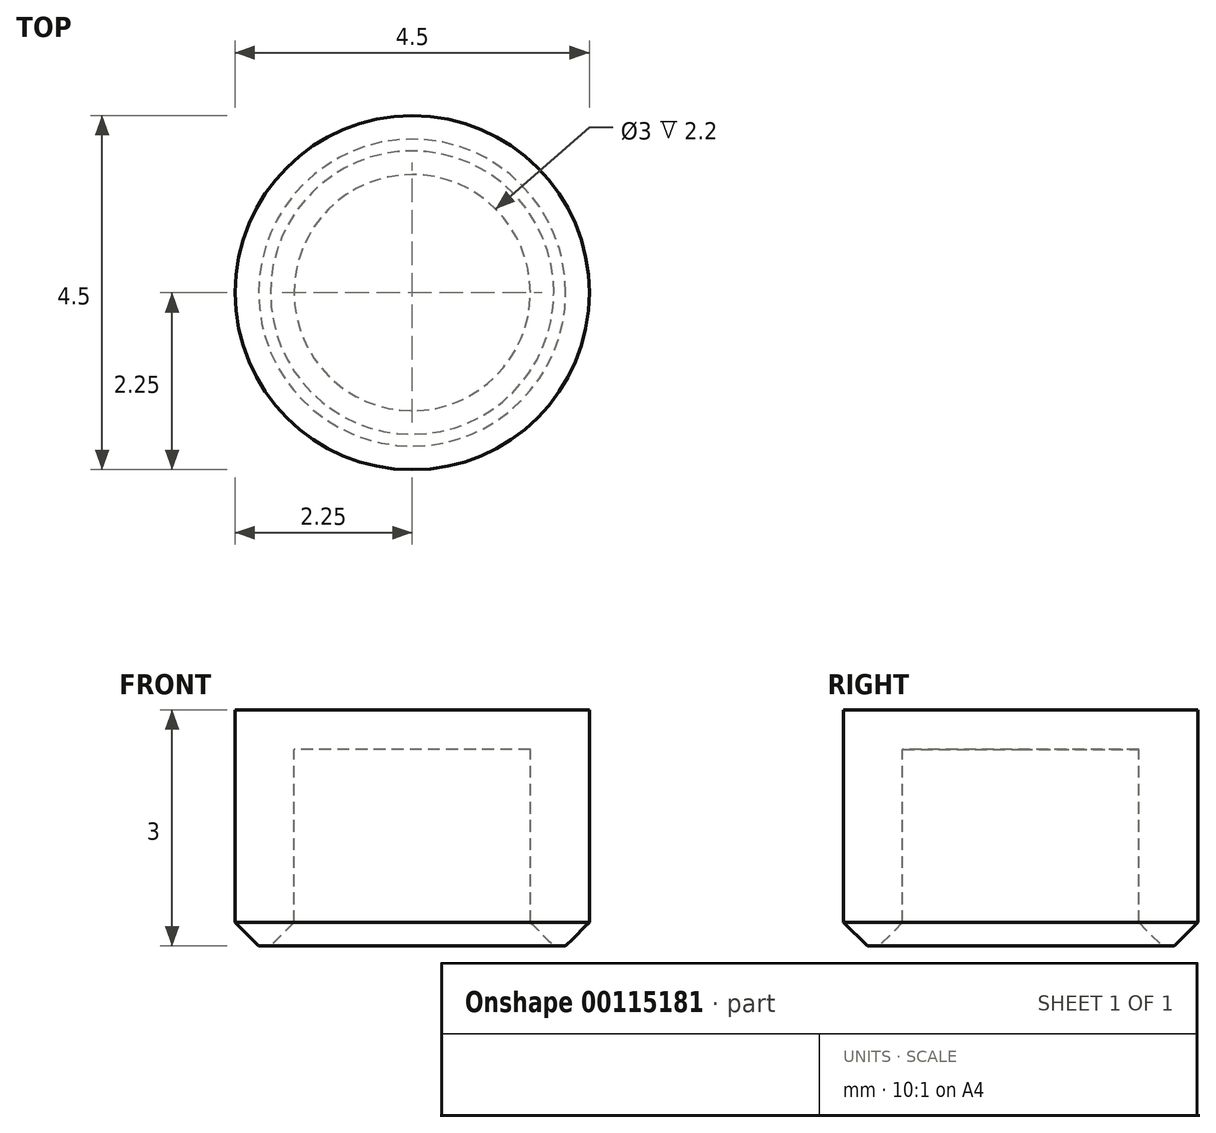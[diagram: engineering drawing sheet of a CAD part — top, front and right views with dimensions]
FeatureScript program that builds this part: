
annotation { "Feature Type Name" : "Feature", "Feature Type Description" : "" }
export const myFeature = defineFeature(function(context is Context, id is Id, definition is map)
    precondition{}
    {
        {
            var Q0;
            Q0=qCreatedBy(makeId("Top.planeOp"),FACE);
            var sketch = newSketch(context, id + "F0", { "sketchPlane" : qUnion([Q0])});
            skCircle(sketch, "E0", {"center": v(0, 0) * mm, "radius": 1.5 * mm});
            skCircle(sketch, "E1", {"center": v(0, 0) * mm, "radius": 2.25 * mm});
            skSolve(sketch);
        }
        {
            var Q0;
            Q0=makeQuery(id+"F0.imprint","IMPRINT",FACE,{"disambiguationData":[TD([[makeQuery(id+"F0.imprint","IMPRINT",EDGE,{"derivedFrom":sQuery(id+"F0.wireOp",EDGE,"E0")}),1.0]])]});
            var Q1;
            Q1=makeQuery(id+"F0.imprint","IMPRINT",FACE,{"disambiguationData":[TD([[makeQuery(id+"F0.imprint","IMPRINT",EDGE,{"derivedFrom":sQuery(id+"F0.wireOp",EDGE,"E0")}),-1.0]])]});
            extrude(context, id + "F1", {"entities" : qUnion([Q0, Q1]), "oppositeDirection" : true, "depth" : 3 * mm});
        }
        {
            var Q0;
            Q0=makeQuery(id+"F0.imprint","IMPRINT",FACE,{"disambiguationData":[TD([[makeQuery(id+"F0.imprint","IMPRINT",EDGE,{"derivedFrom":sQuery(id+"F0.wireOp",EDGE,"E0")}),1.0]])]});
            var Q1;
            Q1=makeQuery(id+"F1.opExtrude","CAP_FACE",FACE,{"disambiguationData":[OSD([sQuery(id+"F0.wireOp",EDGE,"E1")])],"isStart":false});
            var Q2;
            Q2=makeQuery(id+"F1.opExtrude","CAP_FACE",FACE,{"disambiguationData":[OSD([sQuery(id+"F0.wireOp",EDGE,"E1")])],"isStart":false});
            extrude(context, id + "F2", {"entities" : qUnion([Q0]), "operationType" : NewBodyOperationType.REMOVE, "endBound" : BoundingType.UP_TO_SURFACE, "oppositeDirection" : true, "endBoundEntityFace" : qUnion([Q1]), "depth" : 4.28 * mm, "hasSecondDirection" : true, "secondDirectionOppositeDirection" : true, "secondDirectionBoundEntityFace" : qUnion([Q2]), "secondDirectionDepth" : .5 * mm});
        }
        {
            var Q0;
            Q0=makeQuery(id+"F1.opExtrude","CAP_FACE",FACE,{"disambiguationData":[OSD([sQuery(id+"F0.wireOp",EDGE,"E1")])],"isStart":false});
            chamfer(context, id + "F3", {"entities" : qUnion([Q0]), "width" : .3 * mm, "tangentPropagation" : true});
        }
    });
